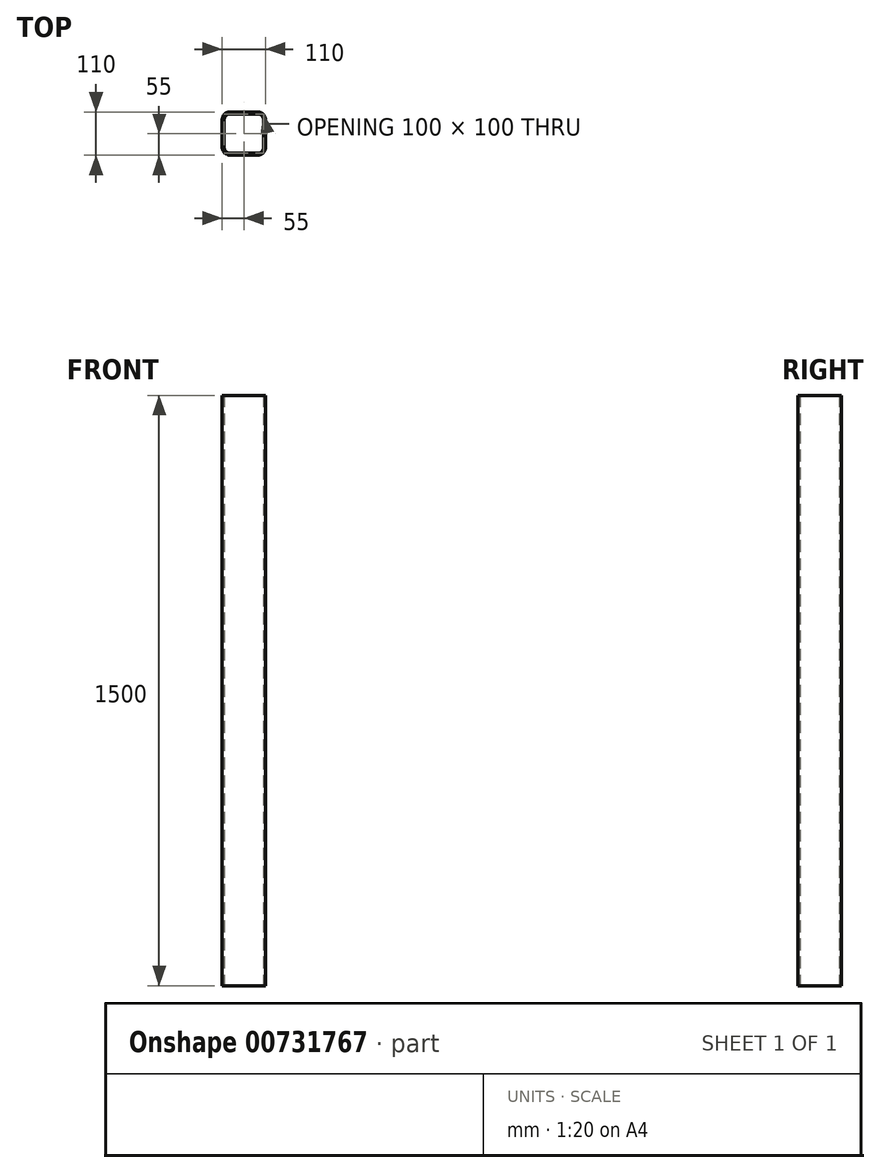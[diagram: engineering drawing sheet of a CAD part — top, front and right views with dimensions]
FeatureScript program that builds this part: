
annotation { "Feature Type Name" : "Feature", "Feature Type Description" : "" }
export const myFeature = defineFeature(function(context is Context, id is Id, definition is map)
    precondition{}
    {
        {
            var Q0;
            Q0=qCreatedBy(makeId("Top.planeOp"),FACE);
            var sketch = newSketch(context, id + "F0", { "sketchPlane" : qUnion([Q0])});
            skLineSegment(sketch, "E0.bottom", {"start": v(35, -50) * mm, "end": v(-35, -50) * mm});
            skLineSegment(sketch, "E0.top", {"start": v(35, 50) * mm, "end": v(-35, 50) * mm});
            skLineSegment(sketch, "E0.left", {"start": v(50, -35) * mm, "end": v(50, 35) * mm});
            skLineSegment(sketch, "E0.right", {"start": v(-50, -35) * mm, "end": v(-50, 35) * mm});
            skPoint(sketch, "E0.middle", {"position": v(0, 0) * mm});
            skPoint(sketch, "E1.visualSharp", {"position": v(-50, 50) * mm});
            skArc(sketch, "E1.filletArc", {"start": v(-35, 50) * mm, "mid": v(-45.6, 45.6) * mm, "end": v(-50, 35) * mm});
            skPoint(sketch, "E2.visualSharp", {"position": v(-50, -50) * mm});
            skArc(sketch, "E2.filletArc", {"start": v(-50, -35) * mm, "mid": v(-45.6, -45.6) * mm, "end": v(-35, -50) * mm});
            skPoint(sketch, "E3.visualSharp", {"position": v(50, -50) * mm});
            skArc(sketch, "E3.filletArc", {"start": v(35, -50) * mm, "mid": v(45.6, -45.6) * mm, "end": v(50, -35) * mm});
            skPoint(sketch, "E4.visualSharp", {"position": v(50, 50) * mm});
            skArc(sketch, "E4.filletArc", {"start": v(50, 35) * mm, "mid": v(45.6, 45.6) * mm, "end": v(35, 50) * mm});
            skArc(sketch, "E5.0", {"start": v(55, 35) * mm, "mid": v(49.14, 49.14) * mm, "end": v(35, 55) * mm});
            skLineSegment(sketch, "E5.1", {"start": v(55, -35) * mm, "end": v(55, 35) * mm});
            skLineSegment(sketch, "E5.2", {"start": v(35, 55) * mm, "end": v(-35, 55) * mm});
            skArc(sketch, "E5.3", {"start": v(35, -55) * mm, "mid": v(49.14, -49.14) * mm, "end": v(55, -35) * mm});
            skArc(sketch, "E5.4", {"start": v(-35, 55) * mm, "mid": v(-49.14, 49.14) * mm, "end": v(-55, 35) * mm});
            skLineSegment(sketch, "E5.5", {"start": v(-55, -35) * mm, "end": v(-55, 35) * mm});
            skArc(sketch, "E5.6", {"start": v(-55, -35) * mm, "mid": v(-49.14, -49.14) * mm, "end": v(-35, -55) * mm});
            skLineSegment(sketch, "E5.7", {"start": v(35, -55) * mm, "end": v(-35, -55) * mm});
            skSolve(sketch);
        }
        {
            var Q0;
            Q0=makeQuery(id+"F0.imprint","IMPRINT",FACE,{"disambiguationData":[TD([[makeQuery(id+"F0.imprint","IMPRINT",EDGE,{"derivedFrom":sQuery(id+"F0.wireOp",EDGE,"E0.bottom")}),1.0]])]});
            extrude(context, id + "F1", {"entities" : qUnion([Q0]), "depth" : 1500 * mm, "offsetDistance" : 25 * mm});
        }
    });
